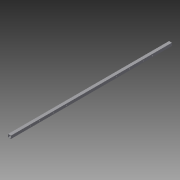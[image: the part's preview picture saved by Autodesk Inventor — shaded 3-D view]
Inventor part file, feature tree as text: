
AUTODESK INVENTOR PART (.ipt)
format: ipt  version: 2015 SP1 (Build 190203100, 203)  size: 110,592 bytes
history: native  units: in
note: dims shown in document units (in); Inventor stores cm internally (conversion verified against a paired STEP export)
features: sketch x4, reference x4, hole x2, extrude x1
ambient origin geometry x8: Origin, YZ Plane, XZ Plane, XY Plane, X Axis, Y Axis, Z Axis, Center Point
bodies: Solid1 (feature_tree)
feature tree (11):
  extrude  "Extrusion1"  Depth=1.0in
  sketch  "Sketch2"  dims[d2=0.12in d3=56.0in]
  hole  "Hole1"  [1 undecoded]
  hole  "Hole2"  [1 undecoded]
  sketch  "Sketch1"  dims[d0=1.0in d1=1.0in]
  sketch  "Sketch3"  dims[d4=0.0in d5=4.5in]
  reference  "Reference1"
  reference  "Reference2"
  reference  "Reference3"
  reference  "Reference4"
  sketch  "Sketch4"  dims[d6=4.75in d7=4.75in d8=4.5in d9=0.2656in d10=0.75in d11=0.375in d12=0.25in d13=0.5635in d14=0.125in d15=0.8108in d16=0.5in d17=0.75in d18=0.375in d19=0.25in d20=0.5635in d21=0.125in d22=0.8108in]
note: 2 required parameter values undecoded (feature->parameter linkage not recoverable at this tier; creation-order binding heuristic only, values carry confidence <= 0.55)
